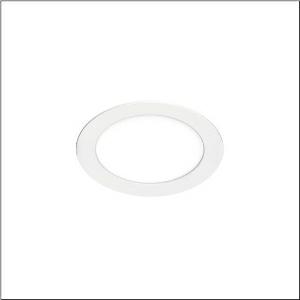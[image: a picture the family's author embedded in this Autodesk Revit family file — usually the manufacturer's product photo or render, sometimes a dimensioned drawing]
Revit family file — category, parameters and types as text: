
# Revit family: lunis_41_flat_51dr107fgca
name_source: partatom
category: Lighting Fixtures
units: mm (PartAtom-declared; Revit-internal decimal feet)

## family parameters
Cut with Voids When Loaded = No
Host = Face
Light Source = No
Part Type = Normal
Room Calculation Point = No
Round Connector Dimension = Use Diameter
Shared = No

## types (1)
- --- (1 x LED, 2160 lm, 22 W, 4000K)
    Apparent Load = 22 VA
    CIE Flux Codes = 49 80 96 100 100
    Color Rendering = 80
    Color Temperature = 4000K
    Default Elevation = 1800 mm
    Description = Lunis 41,  flat, downlight, light emission: direct distribution, LED rated luminous flux: 2.050lm, light colour: 830/840, control gear: ECG, mains connection: 230V, AC, 50/60Hz, housing, round, of aluminium, coated, traffic white (RAL 9016), diameter: 225mm, protection rating (complete): IP20, insulation class (complete): insulation class II (safety insulation), certification: CE, permissible ambient temperature for indoor applications: -20..+40°C, packaging unit: 1 piece
    Height = 0 mm  [stored 0 ft]
    Lamp = 1 x LED
    Lamp Light Flux = 2160 lm
    Lamp Power = 22 W
    Lamp count = 1
    Length = 225 mm
    Luminous efficacy = 98 lm/W
    Manufacturer = Siteco
    ModVariant = No
    Model = 51DR107FGCA
    Mounting Place = Ceiling
    Mounting Type = Recessed
    Number of Poles = 1
    OnlyDefault = Yes
    Power Factor = 1
    Product Name = Lunis 41 flat
    Product group = downlight | ceiling recessed
    ProductGroupID = 402
    Protection Class = Protection class II
    Protection Degree = IP 20
    RLX_Detail_Level = 1
    RlxData = <blob elided: 22189 chars, md5=fc5dbb29>
    Socket = socket
    Standby Power = 0 W
    System Light Flux = 2160 lm
    System Power = 22 W
    Type Comments = factory setting: colour temperature 4000K
    Type Image = l_1007032.jpg
    URL = http://relux.com
    VarID = @adj_117313
    Voltage = 0 V
    Weight = 0.00 kg
    Width = 0 mm  [stored 0 ft]

note: [stored X ft] marks values corroborated as IEEE doubles in the binary element streams (Revit-internal decimal feet)

## geometry (parser evidence)
native form markers: Blend x4, Sweep x12
no freeform markers — native parametric forms only
